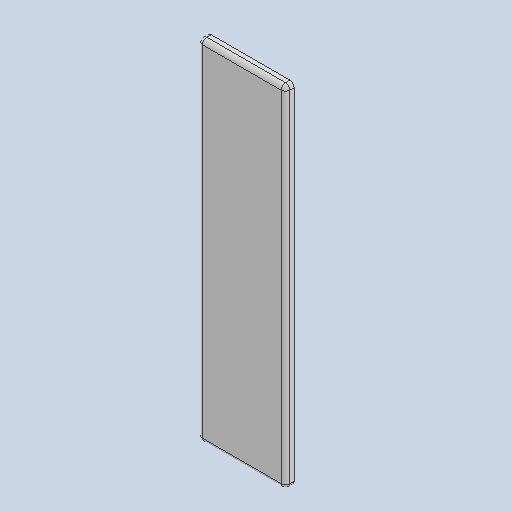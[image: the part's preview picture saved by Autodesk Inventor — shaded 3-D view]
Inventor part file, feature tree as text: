
AUTODESK INVENTOR PART (.ipt)
format: ipt  version: 2022 (Build 260153000, 153)  size: 92,160 bytes
history: native  units: in
note: dims shown in document units (in); Inventor stores cm internally (conversion verified against a paired STEP export)
features: fillet x1
ambient origin geometry x8: Origin, YZ Plane, XZ Plane, XY Plane, X Axis, Y Axis, Z Axis, Center Point
bodies: Solid1 (feature_tree)
feature tree (1):
  fillet  "Fillet2"  [1 undecoded]
note: 1 required parameter value undecoded (feature->parameter linkage not recoverable at this tier; creation-order binding heuristic only, values carry confidence <= 0.55)
